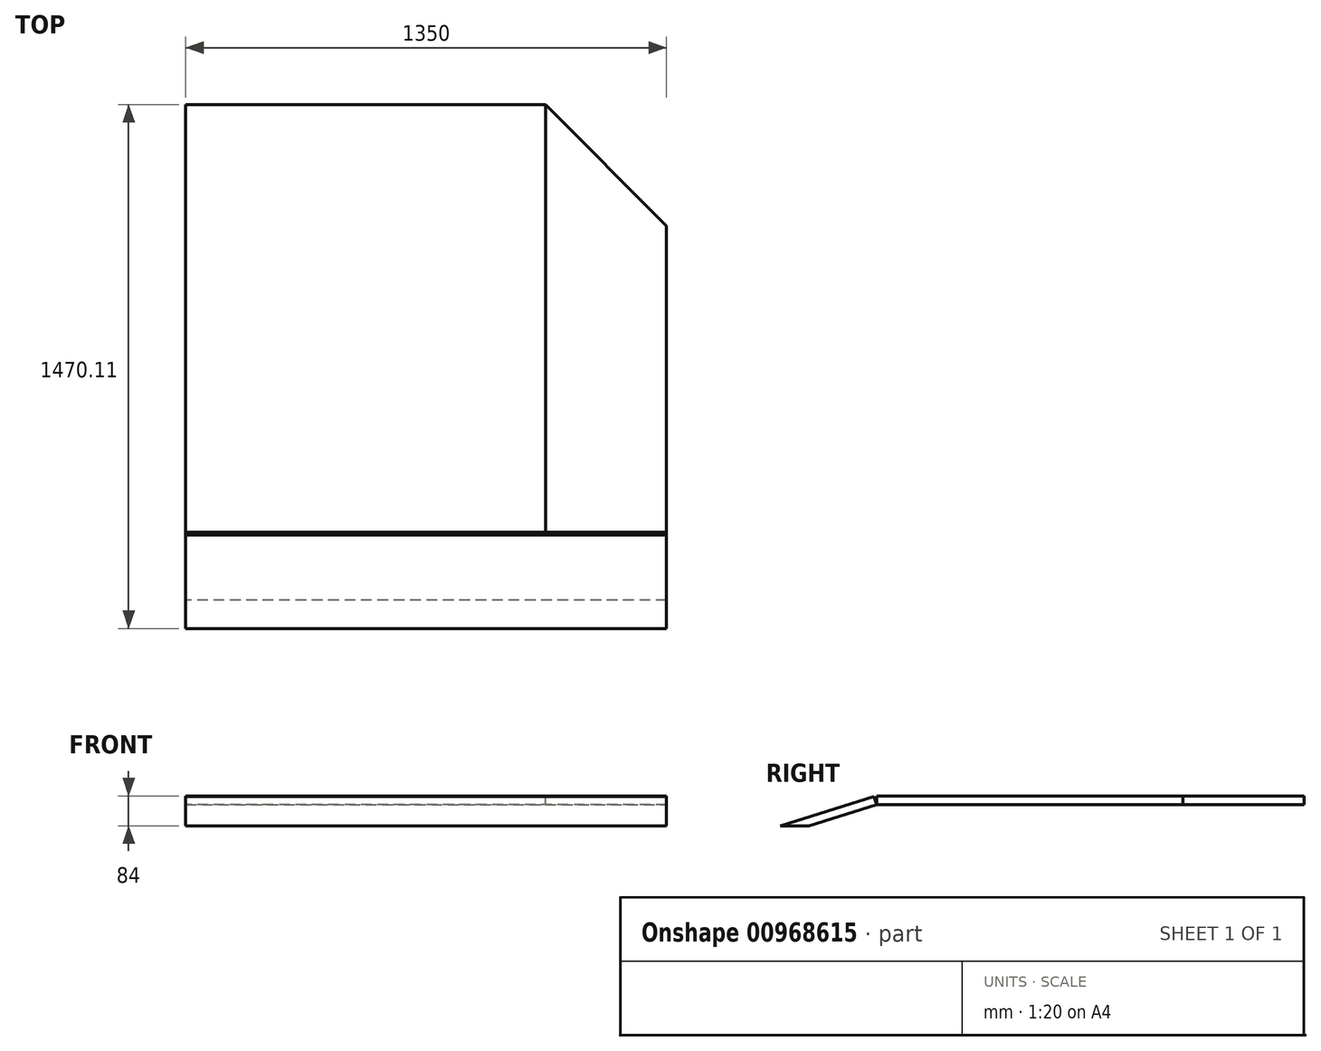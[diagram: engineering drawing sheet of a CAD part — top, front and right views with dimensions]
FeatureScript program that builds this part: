
annotation { "Feature Type Name" : "Feature", "Feature Type Description" : "" }
export const myFeature = defineFeature(function(context is Context, id is Id, definition is map)
    precondition{}
    {
        {
            var Q0;
            Q0=qCreatedBy(makeId("Top.planeOp"),FACE);
            var sketch = newSketch(context, id + "F0", { "sketchPlane" : qUnion([Q0])});
            skLineSegment(sketch, "E0.bottom", {"start": v(0, 0) * mm, "end": v(1010, 0) * mm});
            skLineSegment(sketch, "E0.top", {"start": v(0, -1200) * mm, "end": v(1010, -1200) * mm});
            skLineSegment(sketch, "E0.left", {"start": v(0, 0) * mm, "end": v(0, -1200) * mm});
            skLineSegment(sketch, "E0.right", {"start": v(1010, 0) * mm, "end": v(1010, -1200) * mm});
            skSolve(sketch);
        }
        {
            var Q0;
            Q0=makeQuery(id+"F0.imprint","IMPRINT",FACE,{"disambiguationData":[TD([[makeQuery(id+"F0.imprint","IMPRINT",EDGE,{"derivedFrom":sQuery(id+"F0.wireOp",EDGE,"E0.bottom")}),-1.0]])]});
            extrude(context, id + "F1", {"entities" : qUnion([Q0]), "oppositeDirection" : true, "depth" : 24 * mm, "offsetDistance" : 25 * mm});
        }
        {
            var Q0;
            Q0=qCreatedBy(makeId("Right.planeOp"),FACE);
            var sketch = newSketch(context, id + "F2", { "sketchPlane" : qUnion([Q0])});
            skLineSegment(sketch, "E1", {"start": v(-1200, -24) * mm, "end": v(-1390.3, -84) * mm});
            skLineSegment(sketch, "E2", {"start": v(0, -84) * mm, "end": v(-1390.3, -84) * mm, "construction": true});
            skLineSegment(sketch, "E3", {"start": v(-1200, -24) * mm, "end": v(-1207.22, -1.11) * mm});
            skLineSegment(sketch, "E4", {"start": v(-1207.22, -1.11) * mm, "end": v(-1470.1, -84) * mm});
            skLineSegment(sketch, "E5", {"start": v(-1470.1, -84) * mm, "end": v(-1390.3, -84) * mm});
            skLineSegment(sketch, "E6", {"start": v(-1200, -24) * mm, "end": v(0, -24) * mm});
            skSolve(sketch);
        }
        {
            var Q0;
            Q0=makeQuery(id+"F2.imprint","IMPRINT",FACE,{"disambiguationData":[TD([[makeQuery(id+"F2.imprint","IMPRINT",EDGE,{"derivedFrom":sQuery(id+"F2.wireOp",EDGE,"E1")}),-1.0]])]});
            extrude(context, id + "F3", {"entities" : qUnion([Q0]), "depth" : 1350 * mm, "offsetDistance" : 25 * mm});
        }
        {
            var Q0;
            Q0=qCreatedBy(makeId("Top.planeOp"),FACE);
            var sketch = newSketch(context, id + "F4", { "sketchPlane" : qUnion([Q0])});
            skLineSegment(sketch, "E7.bottom", {"start": v(0, 0) * mm, "end": v(1010, 0) * mm, "construction": true});
            skLineSegment(sketch, "E7.top", {"start": v(0, -1200) * mm, "end": v(1010, -1200) * mm, "construction": true});
            skLineSegment(sketch, "E7.left", {"start": v(0, 0) * mm, "end": v(0, -1200) * mm, "construction": true});
            skLineSegment(sketch, "E7.right", {"start": v(1010, 0) * mm, "end": v(1010, -1200) * mm});
            skLineSegment(sketch, "E8", {"start": v(1010, 0) * mm, "end": v(1350, -340) * mm});
            skLineSegment(sketch, "E9", {"start": v(1350, -340) * mm, "end": v(1350, -1200) * mm});
            skLineSegment(sketch, "E10", {"start": v(1350, -1200) * mm, "end": v(1010, -1200) * mm});
            skSolve(sketch);
        }
        {
            var Q0;
            Q0 = qSketchRegion(id + "F4", true);
            extrude(context, id + "F5", {"entities" : qUnion([Q0]), "oppositeDirection" : true, "depth" : 24 * mm, "offsetDistance" : 25 * mm});
        }
    });
